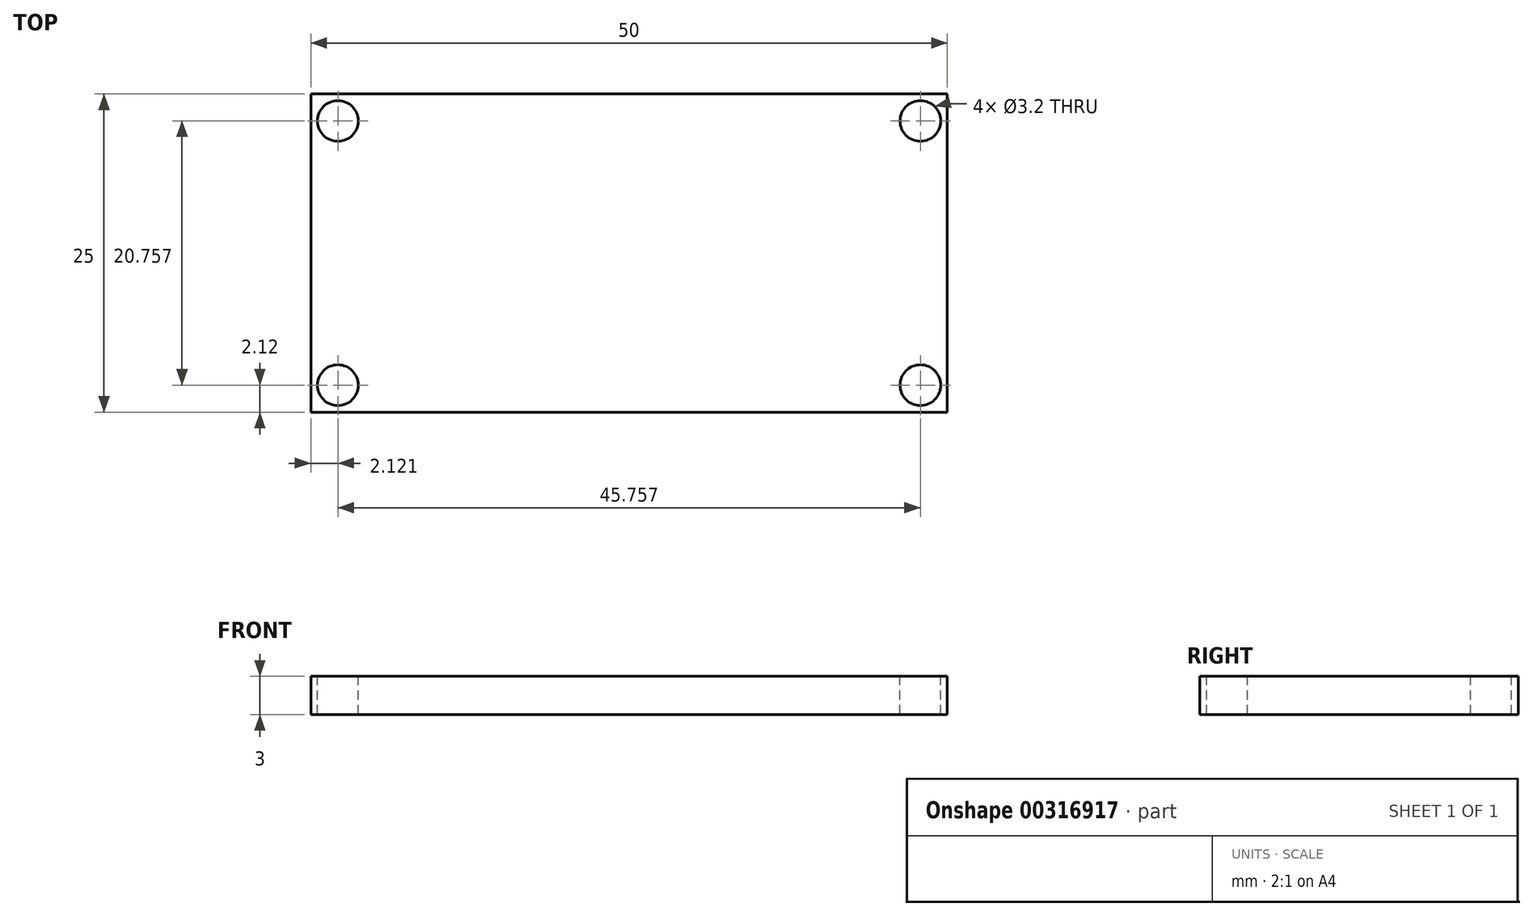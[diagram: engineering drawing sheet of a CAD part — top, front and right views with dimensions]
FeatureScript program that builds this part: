
annotation { "Feature Type Name" : "Feature", "Feature Type Description" : "" }
export const myFeature = defineFeature(function(context is Context, id is Id, definition is map)
    precondition{}
    {
        {
            var Q0;
            Q0=qCreatedBy(makeId("Top.planeOp"),FACE);
            var sketch = newSketch(context, id + "F0", { "sketchPlane" : qUnion([Q0])});
            skLineSegment(sketch, "E0.bottom", {"start": v(0, -1.45) * mm, "end": v(50, -1.45) * mm});
            skLineSegment(sketch, "E0.top", {"start": v(0, 23.55) * mm, "end": v(50, 23.55) * mm});
            skLineSegment(sketch, "E0.left", {"start": v(0, -1.45) * mm, "end": v(0, 23.55) * mm});
            skLineSegment(sketch, "E0.right", {"start": v(50, -1.45) * mm, "end": v(50, 23.55) * mm});
            skSolve(sketch);
        }
        {
            var Q0;
            Q0=makeQuery(id+"F0.imprint","IMPRINT",FACE,{"disambiguationData":[TD([[makeQuery(id+"F0.imprint","IMPRINT",EDGE,{"derivedFrom":sQuery(id+"F0.wireOp",EDGE,"E0.bottom")}),1.0]])]});
            extrude(context, id + "F1", {"entities" : qUnion([Q0]), "depth" : 3 * mm});
        }
        {
            var Q0;
            Q0=makeQuery(id+"F1.opExtrude","CAP_FACE",FACE,{"disambiguationData":[OSD([sQuery(id+"F0.wireOp",EDGE,"E0.bottom"),sQuery(id+"F0.wireOp",EDGE,"E0.top"),sQuery(id+"F0.wireOp",EDGE,"E0.left"),sQuery(id+"F0.wireOp",EDGE,"E0.right")])],"isStart":false});
            var sketch = newSketch(context, id + "F2", { "sketchPlane" : qUnion([Q0])});
            skLineSegment(sketch, "E1", {"start": v(0, 23.55) * mm, "end": v(2.12, 21.43) * mm});
            skLineSegment(sketch, "E2", {"start": v(50, 23.55) * mm, "end": v(47.88, 21.43) * mm});
            skLineSegment(sketch, "E3", {"start": v(50, -1.45) * mm, "end": v(47.88, 0.67) * mm});
            skLineSegment(sketch, "E4", {"start": v(0, -1.45) * mm, "end": v(2.12, 0.67) * mm});
            skSolve(sketch);
        }
        {
            var Q0;
            Q0=sQuery(id+"F2.wireOp",VERTEX,"E1.end");
            var Q1;
            Q1=sQuery(id+"F2.wireOp",VERTEX,"E2.end");
            var Q2;
            Q2=sQuery(id+"F2.wireOp",VERTEX,"E3.end");
            var Q3;
            Q3=sQuery(id+"F2.wireOp",VERTEX,"E4.end");
            var Q4;
            Q4=makeQuery(id+"F1.opExtrude","SWEPT_BODY",BODY,{"disambiguationData":[OSD([sQuery(id+"F0.wireOp",EDGE,"E0.bottom"),sQuery(id+"F0.wireOp",EDGE,"E0.top"),sQuery(id+"F0.wireOp",EDGE,"E0.left"),sQuery(id+"F0.wireOp",EDGE,"E0.right")])]});
            hole(context, id + "F3", {"style" : HoleStyle.SIMPLE, "endStyle" : HoleEndStyle.THROUGH, "holeDiameter" : 3.2 * mm, "isTappedThrough" : true, "tappedDepth" : 12 * mm, "tapClearance" : 3, "locations" : qUnion([Q0, Q1, Q2, Q3]), "scope" : qUnion([Q4])});
        }
    });
